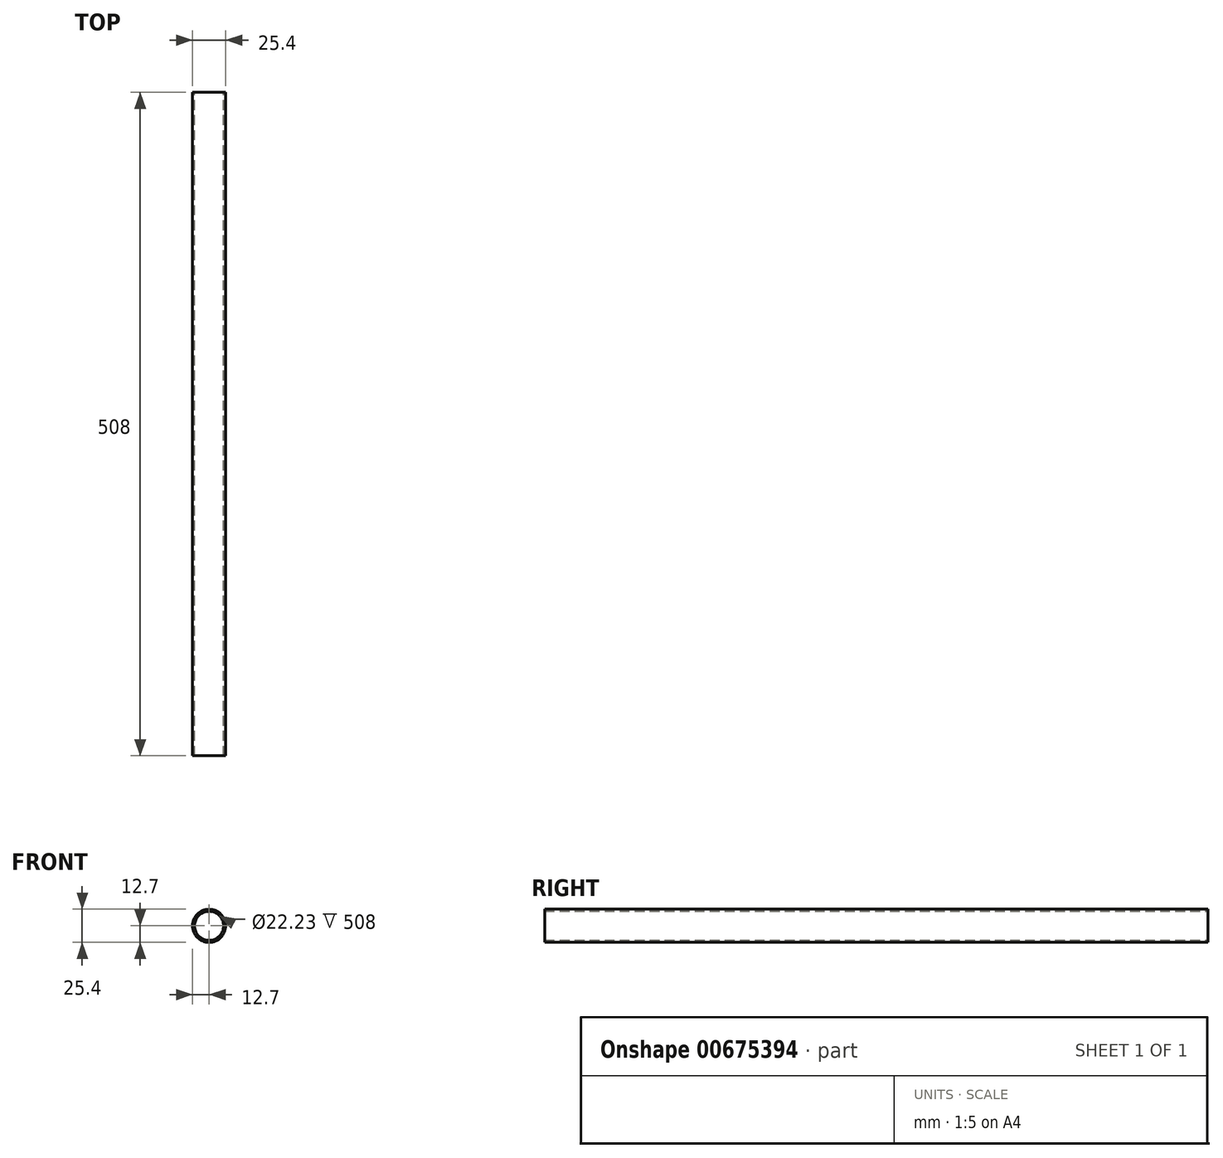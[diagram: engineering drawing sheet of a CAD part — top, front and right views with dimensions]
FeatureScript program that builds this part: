
annotation { "Feature Type Name" : "Feature", "Feature Type Description" : "" }
export const myFeature = defineFeature(function(context is Context, id is Id, definition is map)
    precondition{}
    {
        {
            var Q0;
            Q0=qCreatedBy(makeId("Front.planeOp"),FACE);
            var sketch = newSketch(context, id + "F0", { "sketchPlane" : qUnion([Q0])});
            skCircle(sketch, "E0", {"center": v(0, 0) * mm, "radius": 11.11 * mm});
            skCircle(sketch, "E1", {"center": v(0, 0) * mm, "radius": 12.7 * mm});
            skSolve(sketch);
        }
        {
            var Q0;
            Q0 = qSketchRegion(id + "F0", true);
            extrude(context, id + "F1", {"entities" : qUnion([Q0]), "depth" : 508 * mm, "offsetDistance" : 25.4 * mm});
        }
    });
